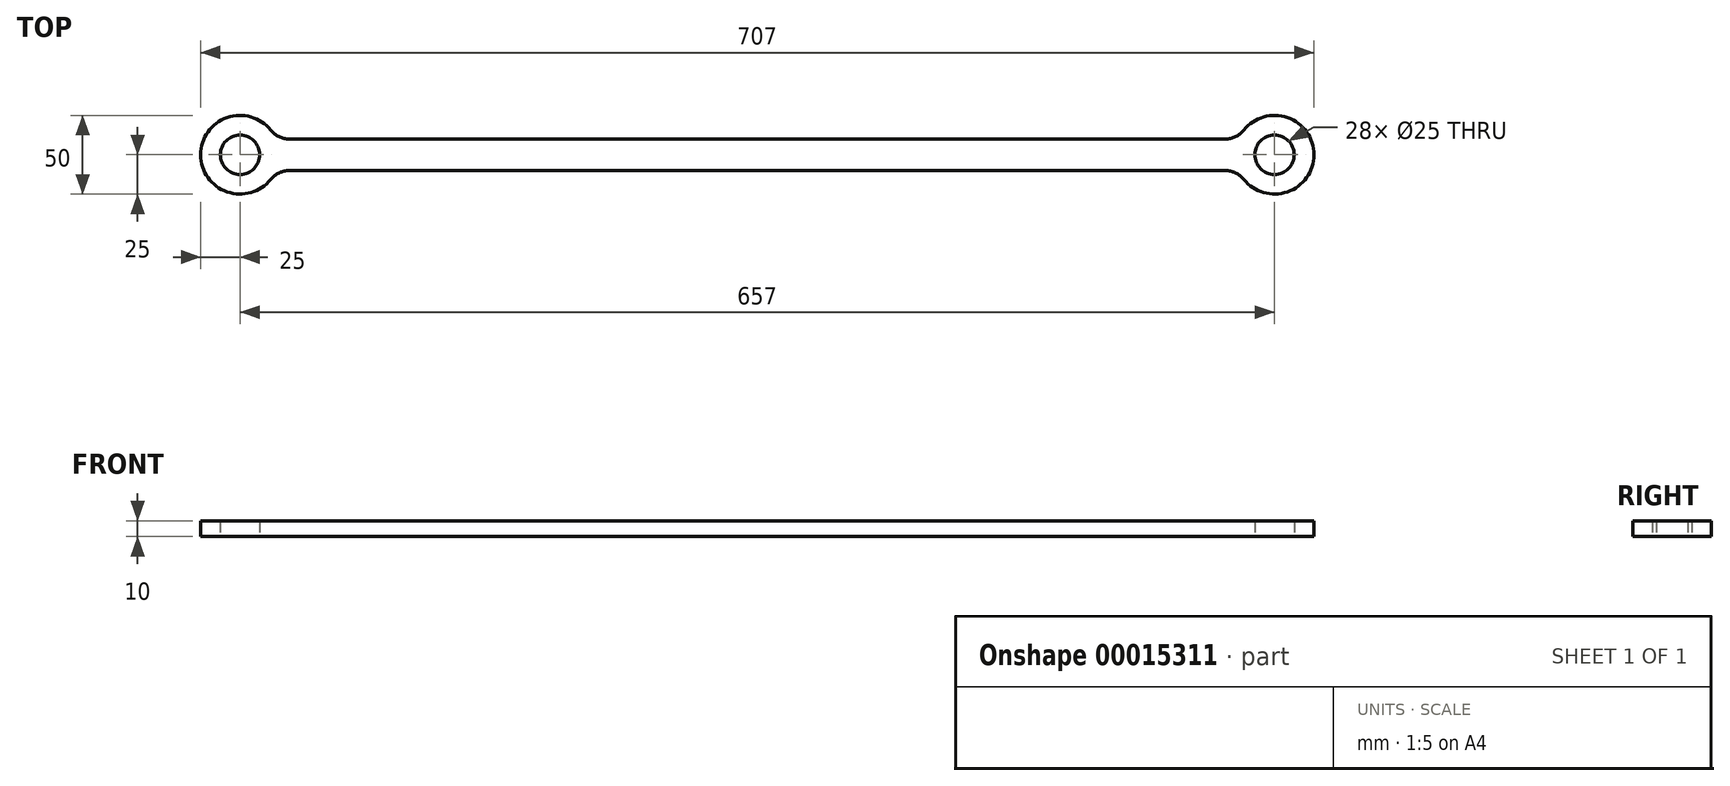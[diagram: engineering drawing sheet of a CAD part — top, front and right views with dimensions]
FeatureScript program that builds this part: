
annotation { "Feature Type Name" : "Feature", "Feature Type Description" : "" }
export const myFeature = defineFeature(function(context is Context, id is Id, definition is map)
    precondition{}
    {
        {
            var Q0;
            Q0=qCreatedBy(makeId("Top.planeOp"),FACE);
            var sketch = newSketch(context, id + "F0", { "sketchPlane" : qUnion([Q0])});
            skArc(sketch, "E0", {"start": v(19.52, 15.63) * mm, "mid": v(-25, 0) * mm, "end": v(19.52, -15.63) * mm});
            skArc(sketch, "E1", {"start": v(637.48, -15.63) * mm, "mid": v(682, 0) * mm, "end": v(637.48, 15.63) * mm});
            skLineSegment(sketch, "E2", {"start": v(31.22, 10) * mm, "end": v(625.78, 10) * mm});
            skLineSegment(sketch, "E3", {"start": v(0, 0) * mm, "end": v(657, 0) * mm, "construction": true});
            skLineSegment(sketch, "E4.MirrorCS", {"start": v(31.22, -10) * mm, "end": v(625.78, -10) * mm});
            skPoint(sketch, "E5.visualSharp", {"position": v(22.91, 10) * mm});
            skArc(sketch, "E5.filletArc", {"start": v(19.52, 15.62) * mm, "mid": v(24.73, 11.48) * mm, "end": v(31.22, 10) * mm});
            skPoint(sketch, "E6.visualSharp", {"position": v(22.91, -10) * mm});
            skArc(sketch, "E6.filletArc", {"start": v(31.22, -10) * mm, "mid": v(24.73, -11.48) * mm, "end": v(19.52, -15.62) * mm});
            skPoint(sketch, "E7.visualSharp", {"position": v(634.09, -10) * mm});
            skArc(sketch, "E7.filletArc", {"start": v(637.48, -15.63) * mm, "mid": v(632.27, -11.48) * mm, "end": v(625.78, -10) * mm});
            skPoint(sketch, "E8.visualSharp", {"position": v(634.09, 10) * mm});
            skArc(sketch, "E8.filletArc", {"start": v(625.78, 10) * mm, "mid": v(632.27, 11.48) * mm, "end": v(637.48, 15.63) * mm});
            skCircle(sketch, "E9", {"center": v(0, 0) * mm, "radius": 12.5 * mm});
            skCircle(sketch, "E10", {"center": v(657, 0) * mm, "radius": 12.5 * mm});
            skSolve(sketch);
        }
        {
            var Q0;
            Q0=qSketchRegion(id+"F0",true);
            extrude(context, id + "F1", {"entities" : qUnion([Q0]), "depth" : 10 * mm});
        }
    });
